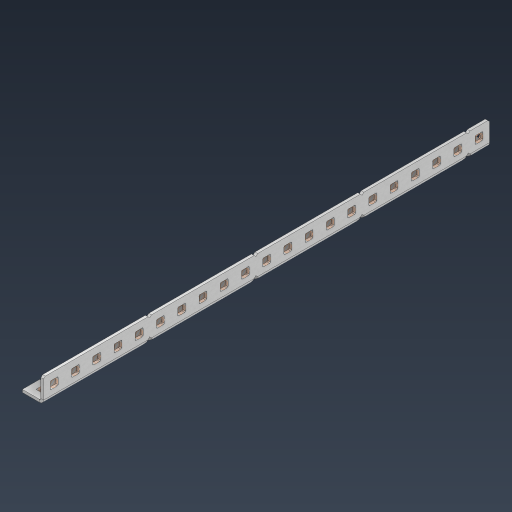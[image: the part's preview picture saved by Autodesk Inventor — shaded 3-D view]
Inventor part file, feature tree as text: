
AUTODESK INVENTOR PART (.ipt)
format: ipt  version: 2024.3 (Build 283343000, 343)  size: 900,608 bytes
history: native  units: in
note: dims shown in document units (in); Inventor stores cm internally (conversion verified against a paired STEP export)
features: other x70, extrude x61, sheet_metal_op x11, pattern_linear x2, mirror x1, chamfer x1, sketch x1
ambient origin geometry x8: Origin, YZ Plane, XZ Plane, XY Plane, X Axis, Y Axis, Z Axis, Center Point
bodies: Solid1 (feature_tree), Body (feature_tree)
feature tree (147):
  sheet_metal_op  "Flanges"
  other  "Flange Pattern Plane"
  other  "Flange Pattern Sketch"
  sheet_metal_op  "Flange Pattern"
  sheet_metal_op  "Body Pattern"
  pattern_linear  "Center Pattern"  Spacing1=10.5in  [1 undecoded]
  other  "Arc Length"
  mirror  "Notch Mirror"
  pattern_linear  "Notch Pattern"  Spacing1=0.0625in  [1 undecoded]
  chamfer  "End Chamfer"
  extrude  "Half Cut"  Depth=0.0625in
  other  "Plate1"
  sketch  "Sketch2"  dims[d0=1.0in d1=10.5in d2=0.0625in d3=0.0625in d4=0.0312in d5=0.125in d6=0.0625in d7=0.5in d8=90.0deg d9=0.0312in d10=0.25in d11=0.0625in d12=0.0625in d16=0.182in d17=0.02in d18=0.0625in d19=0.0in d20=0.25in d21=0.25in d38=8.2677in d40=0.5in d41=0.3937in d43=1.0in d46=0.172in d47=1.0in d48=0.0in d49=0.182in d50=0.02in d51=0.25in d52=0.25in d53=0.0625in d54=0.0in d55=0.172in d56=1.0in d57=0.0in d58=0.25in d60=8.2677in d62=0.5in d63=0.3937in d65=0.5in d85=0.1473in d86=0.1782in d88=0.04in d89=0.0625in d90=0.0in d91=0.04in d92=0.0491in d95=2.5in d96=0.04in d97=0.25in d98=45.0deg d99=0.25in d100=0.5in d101=0.0in d102=2.497in d106=0.182in d107=0.02in d108=0.5in d109=0.5in d110=0.0625in d111=0.0in d112=0.172in d113=0.5in d114=0.0in d117=0.5in d118=0.5in d119=0.5in]
  other  "Plate2"
  sheet_metal_op  "Bend1"
  sheet_metal_op  "Corner1"
  other  "Srf1"
  other  "Srf2"
  other  "Srf91"
  sheet_metal_op  "Body Pattern Sketch"
  other  "Srf92"
  other  "Srf786"
  other  "Srf823"
  other  "Srf824"
  other  "Srf825"
  other  "Srf826"
  other  "Srf827"
  other  "Srf828"
  other  "Srf829"
  other  "Srf856"
  other  "Srf857"
  other  "Srf858"
  other  "Srf859"
  other  "Srf860"
  other  "Srf861"
  other  "Srf862"
  other  "Srf889"
  other  "Srf890"
  other  "Srf891"
  other  "Srf892"
  other  "Srf893"
  other  "Srf894"
  other  "Srf895"
  other  "Srf896"
  other  "Srf922"
  other  "Srf923"
  other  "Srf924"
  other  "Srf925"
  other  "Srf926"
  other  "Srf959"
  other  "Srf960"
  other  "Srf961"
  other  "Srf962"
  other  "Srf963"
  other  "Srf996"
  other  "Srf997"
  other  "Srf998"
  other  "Srf999"
  other  "Srf1000"
  other  "Srf1143"
  other  "Srf1144"
  other  "Srf1145"
  other  "Srf1146"
  other  "Srf1147"
  other  "Srf1148"
  other  "Srf1149"
  other  "Srf1199"
  other  "Srf1200"
  other  "Srf1201"
  other  "Srf1202"
  other  "Srf1203"
  other  "Srf1204"
  other  "Srf1205"
  other  "Srf1255"
  other  "Srf1256"
  other  "Srf1257"
  other  "Srf1258"
  other  "Srf1259"
  other  "Srf1260"
  other  "Srf1261"
  sheet_metal_op  "Flange Stamp"
  sheet_metal_op  "Flange Circle"
  sheet_metal_op  "Body Stamp"
  sheet_metal_op  "Body Circle"
  other  "Center Stamp"
  other  "Center Circle"
  sheet_metal_op  "Notch"
  extrude  "ExtrusionSrf2"  Depth=0.0312in
  extrude  "ExtrusionSrf92"  Depth=0.5in
  extrude  "ExtrusionSrf823"  Depth=0.0625in
  extrude  "ExtrusionSrf824"  Depth=0.5in TaperAngle=90.0deg
  extrude  "ExtrusionSrf825"  Depth=0.5in
  extrude  "ExtrusionSrf826"  Depth=0.0625in
  extrude  "ExtrusionSrf827"  Depth=0.0625in
  extrude  "ExtrusionSrf828"  Depth=0.182in
  extrude  "ExtrusionSrf829"  Depth=0.02in
  extrude  "ExtrusionSrf856"  Depth=0.0625in
  extrude  "ExtrusionSrf857"  TaperAngle=0.0deg  [1 undecoded]
  extrude  "ExtrusionSrf858"  Depth=0.5in
  extrude  "ExtrusionSrf859"  Depth=0.5in
  extrude  "ExtrusionSrf860"  Depth=0.5in
  extrude  "ExtrusionSrf861"  Depth=0.5in
  extrude  "ExtrusionSrf862"  Depth=1.0in TaperAngle=0.0deg
  extrude  "ExtrusionSrf889"  Depth=0.182in
  extrude  "ExtrusionSrf890"  Depth=0.02in
  extrude  "ExtrusionSrf891"  Depth=0.5in
  extrude  "ExtrusionSrf892"  Depth=0.5in
  extrude  "ExtrusionSrf893"  Depth=0.0625in
  extrude  "ExtrusionSrf894"  TaperAngle=0.0deg  [1 undecoded]
  extrude  "ExtrusionSrf895"  Depth=0.5in
  extrude  "ExtrusionSrf896"  Depth=1.0in TaperAngle=0.0deg
  extrude  "ExtrusionSrf922"  Depth=0.5in
  extrude  "ExtrusionSrf923"  Depth=0.5in
  extrude  "ExtrusionSrf924"  Depth=0.5in
  extrude  "ExtrusionSrf925"  Depth=0.5in
  extrude  "ExtrusionSrf926"  Depth=0.5in
  extrude  "ExtrusionSrf959"  Depth=0.5in
  extrude  "ExtrusionSrf960"  Depth=0.0625in
  extrude  "ExtrusionSrf961"  TaperAngle=0.0deg  [1 undecoded]
  extrude  "ExtrusionSrf962"  Depth=0.5in
  extrude  "ExtrusionSrf963"  Depth=0.5in
  extrude  "ExtrusionSrf996"  Depth=0.5in
  extrude  "ExtrusionSrf997"  Depth=0.5in TaperAngle=45.0deg
  extrude  "ExtrusionSrf998"  Depth=0.5in
  extrude  "ExtrusionSrf999"  Depth=0.5in TaperAngle=0.0deg
  extrude  "ExtrusionSrf1000"  Depth=0.5in
  extrude  "ExtrusionSrf1143"  Depth=0.182in
  extrude  "ExtrusionSrf1144"  Depth=0.02in
  extrude  "ExtrusionSrf1145"  Depth=0.5in
  extrude  "ExtrusionSrf1146"  Depth=0.5in
  extrude  "ExtrusionSrf1147"  Depth=0.0625in
  extrude  "ExtrusionSrf1148"  TaperAngle=0.0deg  [1 undecoded]
  extrude  "ExtrusionSrf1149"  Depth=0.5in
  extrude  "ExtrusionSrf1199"  Depth=0.5in TaperAngle=0.0deg
  extrude  "ExtrusionSrf1200"  Depth=0.5in
  extrude  "ExtrusionSrf1201"  Depth=0.5in
  extrude  "ExtrusionSrf1202"  Depth=0.5in
  extrude  "ExtrusionSrf1203"  [1 undecoded]
  extrude  "ExtrusionSrf1204"  [1 undecoded]
  extrude  "ExtrusionSrf1205"  [1 undecoded]
  extrude  "ExtrusionSrf1255"  [1 undecoded]
  extrude  "ExtrusionSrf1256"  [1 undecoded]
  extrude  "ExtrusionSrf1257"  [1 undecoded]
  extrude  "ExtrusionSrf1258"  [1 undecoded]
  extrude  "ExtrusionSrf1259"  [1 undecoded]
  extrude  "ExtrusionSrf1260"  [1 undecoded]
  extrude  "ExtrusionSrf1261"  [1 undecoded]
note: 16 required parameter values undecoded (feature->parameter linkage not recoverable at this tier; creation-order binding heuristic only, values carry confidence <= 0.55)
